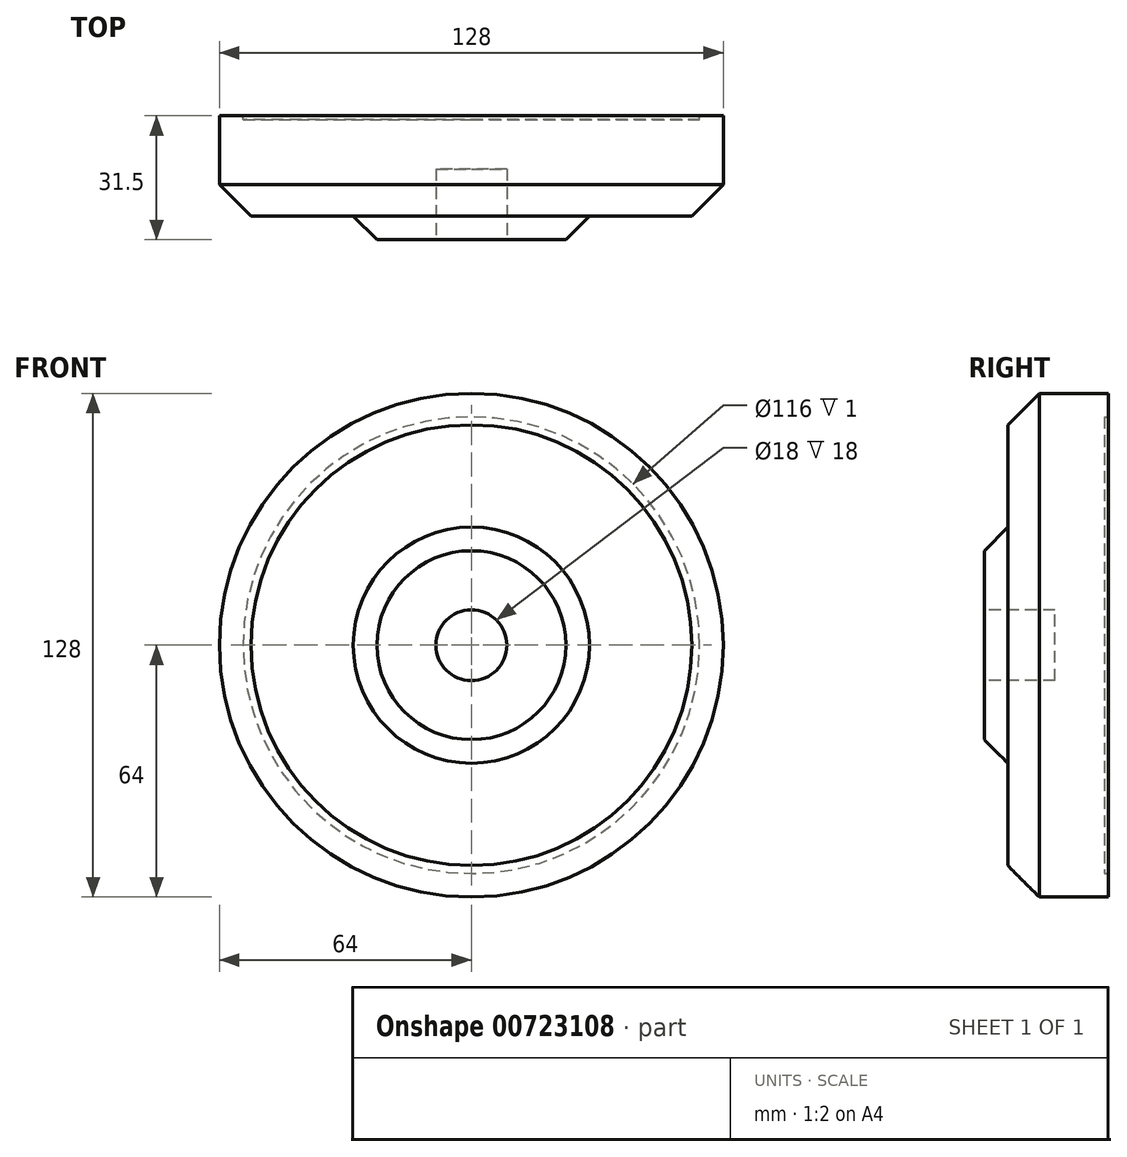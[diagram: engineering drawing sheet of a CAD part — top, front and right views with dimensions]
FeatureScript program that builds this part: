
annotation { "Feature Type Name" : "Feature", "Feature Type Description" : "" }
export const myFeature = defineFeature(function(context is Context, id is Id, definition is map)
    precondition{}
    {
        {
            var Q0;
            Q0=qCreatedBy(makeId("Front.planeOp"),FACE);
            var sketch = newSketch(context, id + "F0", { "sketchPlane" : qUnion([Q0])});
            skCircle(sketch, "E0", {"center": v(0, 0) * mm, "radius": 64 * mm});
            skSolve(sketch);
        }
        {
            var Q0;
            Q0=qSketchRegion(id+"F0",true);
            extrude(context, id + "F1", {"entities" : qUnion([Q0]), "depth" : 25.5 * mm, "offsetDistance" : 25 * mm});
        }
        {
            var Q0;
            Q0=makeQuery(id+"F1.opExtrude","CAP_FACE",FACE,{"disambiguationData":[OSD([sQuery(id+"F0.wireOp",EDGE,"E0")])],"isStart":true});
            var sketch = newSketch(context, id + "F2", { "sketchPlane" : qUnion([Q0])});
            skCircle(sketch, "E1", {"center": v(0, 0) * mm, "radius": 58 * mm});
            skSolve(sketch);
        }
        {
            var Q0;
            Q0=qSketchRegion(id+"F2",true);
            extrude(context, id + "F3", {"entities" : qUnion([Q0]), "operationType" : NewBodyOperationType.REMOVE, "oppositeDirection" : true, "depth" : 1 * mm, "offsetDistance" : 25 * mm});
        }
        {
            var Q0;
            Q0=makeQuery(id+"F1.opExtrude","CAP_EDGE",EDGE,{"disambiguationData":[OSD([sQuery(id+"F0.wireOp",EDGE,"E0")])],"isStart":false});
            chamfer(context, id + "F4", {"entities" : qUnion([Q0]), "width" : 8 * mm, "tangentPropagation" : true});
        }
        {
            var Q0;
            Q0=makeQuery(id+"F1.opExtrude","CAP_FACE",FACE,{"disambiguationData":[OSD([sQuery(id+"F0.wireOp",EDGE,"E0")])],"isStart":false});
            var sketch = newSketch(context, id + "F5", { "sketchPlane" : qUnion([Q0])});
            skCircle(sketch, "E2", {"center": v(0, 0) * mm, "radius": 30 * mm});
            skSolve(sketch);
        }
        {
            var Q0;
            Q0=makeQuery(id+"F5.imprint","IMPRINT",FACE,{"disambiguationData":[TD([[makeQuery(id+"F5.imprint","IMPRINT",EDGE,{"derivedFrom":sQuery(id+"F5.wireOp",EDGE,"E2")}),1.0]])]});
            extrude(context, id + "F6", {"entities" : qUnion([Q0]), "operationType" : NewBodyOperationType.ADD, "depth" : 6 * mm, "offsetDistance" : 25 * mm});
        }
        {
            var Q0;
            Q0=makeQuery(id+"F6.opExtrude","CAP_EDGE",EDGE,{"disambiguationData":[OSD([sQuery(id+"F5.wireOp",EDGE,"E2")])],"isStart":false});
            chamfer(context, id + "F7", {"entities" : qUnion([Q0]), "width" : 6 * mm, "tangentPropagation" : true});
        }
        {
            var Q0;
            Q0=makeQuery(id+"F6.opExtrude","CAP_FACE",FACE,{"disambiguationData":[OSD([sQuery(id+"F5.wireOp",EDGE,"E2")])],"isStart":false});
            var sketch = newSketch(context, id + "F8", { "sketchPlane" : qUnion([Q0])});
            skPoint(sketch, "E3", {"position": v(0, 0) * mm});
            skSolve(sketch);
        }
        {
            var Q0;
            {var subQ0=sQuery(id+"F5.wireOp",EDGE,"E2");Q0=makeQuery(id+"F8.imprint","IMPRINT",FACE,{"disambiguationData":[TD([[makeQuery(id+"F8.imprint","IMPRINT",EDGE,{"derivedFrom":makeQuery(id+"F7.opChamfer","BLEND_EDGE",EDGE,{"blendedFrom":[makeQuery(id+"F6.opExtrude","CAP_EDGE",EDGE,{"disambiguationData":[OSD([subQ0])],"isStart":false}),makeQuery(id+"F6.opExtrude","CAP_FACE",FACE,{"disambiguationData":[OSD([subQ0])],"isStart":false})],"blendedInto":[makeQuery(id+"F6.opExtrude","CAP_FACE",FACE,{"disambiguationData":[OSD([subQ0])],"isStart":false})]})}),1.0]])]});}
            var sketch = newSketch(context, id + "F9", { "sketchPlane" : qUnion([Q0])});
            skCircle(sketch, "E4", {"center": v(0, 0) * mm, "radius": 9 * mm});
            skSolve(sketch);
        }
        {
            var Q0;
            Q0=qSketchRegion(id+"F9",true);
            extrude(context, id + "F10", {"entities" : qUnion([Q0]), "operationType" : NewBodyOperationType.REMOVE, "oppositeDirection" : true, "depth" : 18 * mm, "offsetDistance" : 25 * mm});
        }
    });
